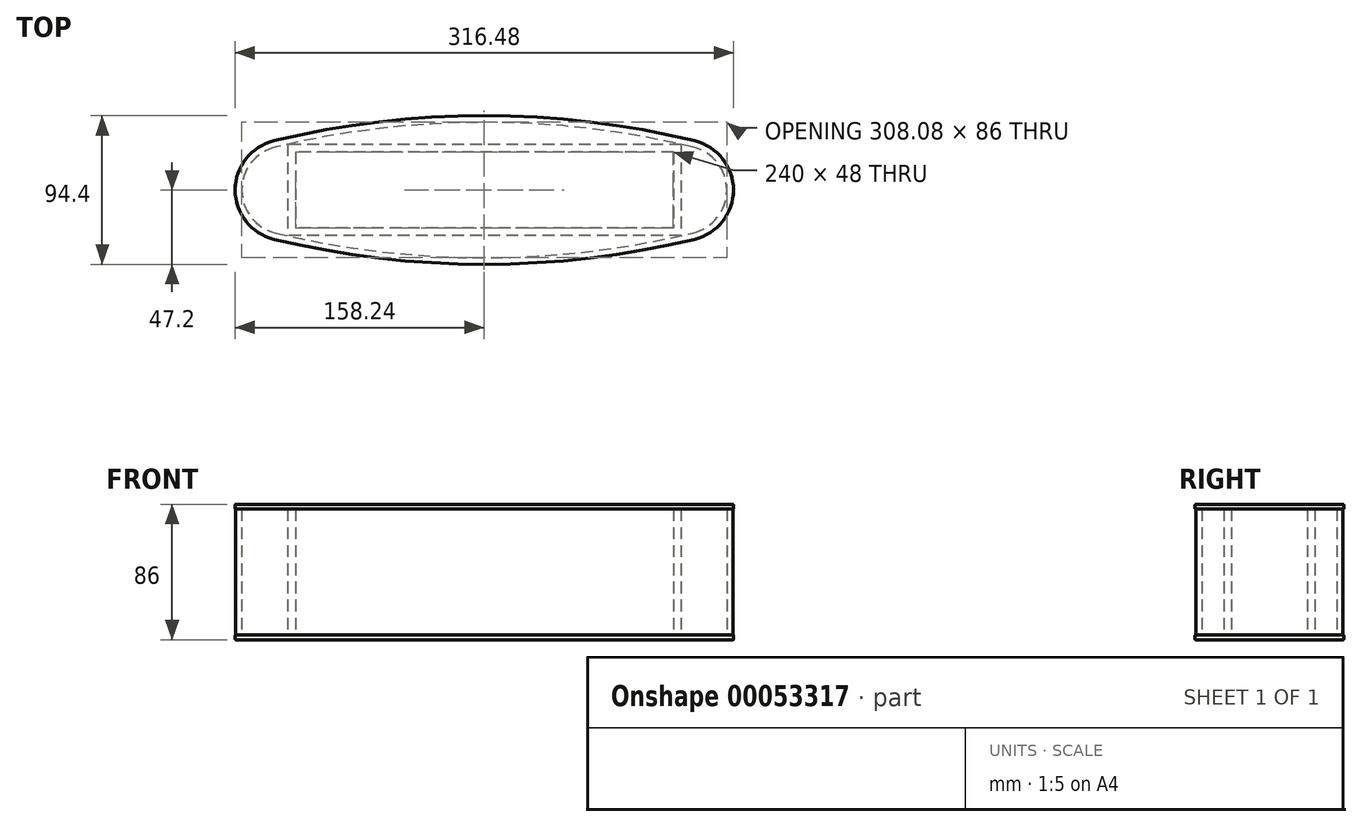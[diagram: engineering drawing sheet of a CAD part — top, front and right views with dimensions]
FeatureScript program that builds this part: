
annotation { "Feature Type Name" : "Feature", "Feature Type Description" : "" }
export const myFeature = defineFeature(function(context is Context, id is Id, definition is map)
    precondition{}
    {
        {
            var Q0;
            Q0=qCreatedBy(makeId("Top.planeOp"),FACE);
            var sketch = newSketch(context, id + "F0", { "sketchPlane" : qUnion([Q0])});
            skLineSegment(sketch, "E0.rect.bottom", {"start": v(120, 24) * mm, "end": v(-120, 24) * mm});
            skLineSegment(sketch, "E0.rect.top", {"start": v(120, -24) * mm, "end": v(-120, -24) * mm});
            skLineSegment(sketch, "E0.rect.left", {"start": v(120, 24) * mm, "end": v(120, -24) * mm});
            skLineSegment(sketch, "E0.rect.right", {"start": v(-120, 24) * mm, "end": v(-120, -24) * mm});
            skPoint(sketch, "E0.rect.middle", {"position": v(0, 0) * mm});
            skLineSegment(sketch, "E1.rect.bottom", {"start": v(125, 29) * mm, "end": v(-125, 29) * mm});
            skLineSegment(sketch, "E1.rect.top", {"start": v(125, -29) * mm, "end": v(-125, -29) * mm});
            skLineSegment(sketch, "E1.rect.left", {"start": v(125, 29) * mm, "end": v(125, -29) * mm});
            skLineSegment(sketch, "E1.rect.right", {"start": v(-125, 29) * mm, "end": v(-125, -29) * mm});
            skArc(sketch, "E2", {"start": v(132.61, 27.22) * mm, "mid": v(0, 43) * mm, "end": v(-132.61, 27.22) * mm});
            skArc(sketch, "E3", {"start": v(-132.61, -27.22) * mm, "mid": v(0, -43) * mm, "end": v(132.61, -27.22) * mm});
            skArc(sketch, "E4", {"start": v(-132.61, 27.22) * mm, "mid": v(-154.04, 0) * mm, "end": v(-132.61, -27.22) * mm});
            skArc(sketch, "E5", {"start": v(132.61, -27.22) * mm, "mid": v(154.04, 0) * mm, "end": v(132.61, 27.22) * mm});
            skArc(sketch, "E6.0", {"start": v(133.5, 30.91) * mm, "mid": v(0, 46.8) * mm, "end": v(-133.5, 30.91) * mm});
            skArc(sketch, "E6.1", {"start": v(133.5, -30.91) * mm, "mid": v(157.84, 0) * mm, "end": v(133.5, 30.91) * mm});
            skArc(sketch, "E6.2", {"start": v(-133.5, -30.91) * mm, "mid": v(0, -46.8) * mm, "end": v(133.5, -30.91) * mm});
            skArc(sketch, "E6.3", {"start": v(-133.5, 30.91) * mm, "mid": v(-157.84, 0) * mm, "end": v(-133.5, -30.91) * mm});
            skArc(sketch, "E7.0", {"start": v(133.6, 31.3) * mm, "mid": v(0, 47.2) * mm, "end": v(-133.6, 31.3) * mm});
            skArc(sketch, "E7.1", {"start": v(133.6, -31.3) * mm, "mid": v(158.24, 0) * mm, "end": v(133.6, 31.3) * mm});
            skArc(sketch, "E7.2", {"start": v(-133.6, -31.3) * mm, "mid": v(0, -47.2) * mm, "end": v(133.6, -31.3) * mm});
            skArc(sketch, "E7.3", {"start": v(-133.6, 31.3) * mm, "mid": v(-158.24, 0) * mm, "end": v(-133.6, -31.3) * mm});
            skSolve(sketch);
        }
        {
            var Q0;
            {var subQ5=sQuery(id+"F0.wireOp",EDGE,"E4");Q0=makeQuery(id+"F0.imprint","IMPRINT",FACE,{"disambiguationData":[TD([[makeQuery(id+"F0.imprint","IMPRINT",EDGE,{"derivedFrom":subQ5}),-1.0]])]});}
            var Q1;
            Q1=makeQuery(id+"F0.imprint","IMPRINT",FACE,{"disambiguationData":[TD([[makeQuery(id+"F0.imprint","IMPRINT",EDGE,{"derivedFrom":sQuery(id+"F0.wireOp",EDGE,"E0.rect.bottom")}),-1.0]])]});
            extrude(context, id + "F1", {"entities" : qUnion([Q0, Q1]), "depth" : 80 * mm});
        }
        {
            var Q0;
            Q0 = qSketchRegion(id + "F0", true);
            var Q1;
            Q1=makeQuery(id+"F1.opExtrude","CAP_FACE",FACE,{"disambiguationData":[OSD([sQuery(id+"F0.wireOp",EDGE,"E2"),sQuery(id+"F0.wireOp",EDGE,"E3"),sQuery(id+"F0.wireOp",EDGE,"E4"),sQuery(id+"F0.wireOp",EDGE,"E5"),sQuery(id+"F0.wireOp",EDGE,"E6.0"),sQuery(id+"F0.wireOp",EDGE,"E6.1"),sQuery(id+"F0.wireOp",EDGE,"E6.2"),sQuery(id+"F0.wireOp",EDGE,"E6.3")])],"isStart":true});
            var Q2;
            {var subQ0=sQuery(id+"F0.wireOp",EDGE,"E1.rect.left");Q2=makeQuery(id+"F0.imprint","IMPRINT",FACE,{"disambiguationData":[TD([[makeQuery(id+"F0.imprint","IMPRINT",EDGE,{"derivedFrom":subQ0}),1.0]])]});}
            var Q3;
            {var subQ0=sQuery(id+"F0.wireOp",EDGE,"E1.rect.bottom");Q3=makeQuery(id+"F0.imprint","IMPRINT",FACE,{"disambiguationData":[TD([[makeQuery(id+"F0.imprint","IMPRINT",EDGE,{"derivedFrom":subQ0}),-1.0]])]});}
            var Q4;
            Q4=makeQuery(id+"F0.imprint","IMPRINT",FACE,{"disambiguationData":[TD([[makeQuery(id+"F0.imprint","IMPRINT",EDGE,{"derivedFrom":sQuery(id+"F0.wireOp",EDGE,"E0.rect.bottom")}),-1.0]])]});
            var Q5;
            Q5=makeQuery(id+"F0.imprint","IMPRINT",FACE,{"disambiguationData":[TD([[makeQuery(id+"F0.imprint","IMPRINT",EDGE,{"derivedFrom":sQuery(id+"F0.wireOp",EDGE,"E0.rect.bottom")}),1.0]])]});
            var Q6;
            {var subQ0=sQuery(id+"F0.wireOp",EDGE,"E1.rect.top");Q6=makeQuery(id+"F0.imprint","IMPRINT",FACE,{"disambiguationData":[TD([[makeQuery(id+"F0.imprint","IMPRINT",EDGE,{"derivedFrom":subQ0}),1.0]])]});}
            var Q7;
            {var subQ0=sQuery(id+"F0.wireOp",EDGE,"E1.rect.right");Q7=makeQuery(id+"F0.imprint","IMPRINT",FACE,{"disambiguationData":[TD([[makeQuery(id+"F0.imprint","IMPRINT",EDGE,{"derivedFrom":subQ0}),-1.0]])]});}
            extrude(context, id + "F2", {"entities" : qUnion([Q0, Q1, Q2, Q3, Q4, Q5, Q6, Q7]), "oppositeDirection" : true, "depth" : 3 * mm});
        }
        {
            var Q0;
            Q0=makeQuery(id+"F2.opExtrude","SWEPT_BODY",BODY,{"disambiguationData":[OSD([sQuery(id+"F0.wireOp",EDGE,"E2"),sQuery(id+"F0.wireOp",EDGE,"E3"),sQuery(id+"F0.wireOp",EDGE,"E4"),sQuery(id+"F0.wireOp",EDGE,"E5"),sQuery(id+"F0.wireOp",EDGE,"E6.0"),sQuery(id+"F0.wireOp",EDGE,"E6.1"),sQuery(id+"F0.wireOp",EDGE,"E6.2"),sQuery(id+"F0.wireOp",EDGE,"E6.3")])]});
            var Q1;
            Q1=makeQuery(id+"F2.opExtrude","SWEPT_BODY",BODY,{"disambiguationData":[OSD([sQuery(id+"F0.wireOp",EDGE,"E6.0"),sQuery(id+"F0.wireOp",EDGE,"E6.1"),sQuery(id+"F0.wireOp",EDGE,"E6.2"),sQuery(id+"F0.wireOp",EDGE,"E6.3"),sQuery(id+"F0.wireOp",EDGE,"E7.0"),sQuery(id+"F0.wireOp",EDGE,"E7.1"),sQuery(id+"F0.wireOp",EDGE,"E7.2"),sQuery(id+"F0.wireOp",EDGE,"E7.3")])]});
            booleanBodies(context, id + "F3", {"operationType" : BooleanOperationType.UNION, "tools" : qUnion([Q0, Q1])});
        }
        {
            var Q0;
            Q0=makeQuery(id+"F2.opExtrude","SWEPT_BODY",BODY,{"disambiguationData":[OSD([sQuery(id+"F0.wireOp",EDGE,"E2"),sQuery(id+"F0.wireOp",EDGE,"E3"),sQuery(id+"F0.wireOp",EDGE,"E4"),sQuery(id+"F0.wireOp",EDGE,"E5")])]});
            var Q1;
            Q1=makeQuery(id+"F2.opExtrude","SWEPT_BODY",BODY,{"disambiguationData":[OSD([sQuery(id+"F0.wireOp",EDGE,"E2"),sQuery(id+"F0.wireOp",EDGE,"E3"),sQuery(id+"F0.wireOp",EDGE,"E4"),sQuery(id+"F0.wireOp",EDGE,"E5"),sQuery(id+"F0.wireOp",EDGE,"E6.0"),sQuery(id+"F0.wireOp",EDGE,"E6.1"),sQuery(id+"F0.wireOp",EDGE,"E6.2"),sQuery(id+"F0.wireOp",EDGE,"E6.3")])]});
            booleanBodies(context, id + "F4", {"operationType" : BooleanOperationType.UNION, "tools" : qUnion([Q0, Q1])});
        }
        {
            var Q0;
            Q0=makeQuery(id+"F1.opExtrude","CAP_FACE",FACE,{"disambiguationData":[OSD([sQuery(id+"F0.wireOp",EDGE,"E2"),sQuery(id+"F0.wireOp",EDGE,"E3"),sQuery(id+"F0.wireOp",EDGE,"E4"),sQuery(id+"F0.wireOp",EDGE,"E5"),sQuery(id+"F0.wireOp",EDGE,"E6.0"),sQuery(id+"F0.wireOp",EDGE,"E6.1"),sQuery(id+"F0.wireOp",EDGE,"E6.2"),sQuery(id+"F0.wireOp",EDGE,"E6.3")])],"isStart":false});
            var sketch = newSketch(context, id + "F5", { "sketchPlane" : qUnion([Q0])});
            skArc(sketch, "E8.0", {"start": v(-133.6, -31.3) * mm, "mid": v(0, -47.2) * mm, "end": v(133.6, -31.3) * mm});
            skArc(sketch, "E9.0", {"start": v(133.6, -31.3) * mm, "mid": v(158.24, 0) * mm, "end": v(133.6, 31.3) * mm});
            skArc(sketch, "E10.0", {"start": v(-133.6, 31.3) * mm, "mid": v(-158.24, 0) * mm, "end": v(-133.6, -31.3) * mm});
            skArc(sketch, "E11.0", {"start": v(133.6, 31.3) * mm, "mid": v(0, 47.2) * mm, "end": v(-133.6, 31.3) * mm});
            skSolve(sketch);
        }
        {
            var Q0;
            Q0 = qSketchRegion(id + "F5", true);
            extrude(context, id + "F6", {"entities" : qUnion([Q0]), "depth" : 3 * mm});
        }
        {
            var Q0;
            Q0=makeQuery(id+"F6.opExtrude","CAP_FACE",FACE,{"disambiguationData":[OSD([sQuery(id+"F5.wireOp",EDGE,"E8.0"),sQuery(id+"F5.wireOp",EDGE,"E9.0"),sQuery(id+"F5.wireOp",EDGE,"E10.0"),sQuery(id+"F5.wireOp",EDGE,"E11.0")])],"isStart":false});
            var Q1;
            {var subQ0=sQuery(id+"F0.wireOp",EDGE,"E6.3");var subQ1=sQuery(id+"F0.wireOp",EDGE,"E6.2");var subQ2=sQuery(id+"F0.wireOp",EDGE,"E6.1");var subQ3=sQuery(id+"F0.wireOp",EDGE,"E6.0");var subQ4=sQuery(id+"F0.wireOp",EDGE,"E5");var subQ5=sQuery(id+"F0.wireOp",EDGE,"E4");var subQ6=sQuery(id+"F0.wireOp",EDGE,"E3");var subQ7=sQuery(id+"F0.wireOp",EDGE,"E2");Q1=makeQuery(id+"F4.opBoolean","MERGE",FACE,{"derivedFrom":[makeQuery(id+"F2.opExtrude","CAP_FACE",FACE,{"disambiguationData":[OSD([subQ7,subQ6,subQ5,subQ4])],"isStart":true}),makeQuery(id+"F3.opBoolean","MERGE",FACE,{"derivedFrom":[makeQuery(id+"F2.opExtrude","CAP_FACE",FACE,{"disambiguationData":[OSD([subQ3,subQ2,subQ1,subQ0,sQuery(id+"F0.wireOp",EDGE,"E7.0"),sQuery(id+"F0.wireOp",EDGE,"E7.1"),sQuery(id+"F0.wireOp",EDGE,"E7.2"),sQuery(id+"F0.wireOp",EDGE,"E7.3")])],"isStart":true}),makeQuery(id+"F2.opExtrude","CAP_FACE",FACE,{"disambiguationData":[OSD([subQ7,subQ6,subQ5,subQ4,subQ3,subQ2,subQ1,subQ0])],"isStart":true})]})]});}
            var Q2;
            Q2=makeQuery(id+"F6.opExtrude","CAP_FACE",FACE,{"disambiguationData":[OSD([sQuery(id+"F5.wireOp",EDGE,"E8.0"),sQuery(id+"F5.wireOp",EDGE,"E9.0"),sQuery(id+"F5.wireOp",EDGE,"E10.0"),sQuery(id+"F5.wireOp",EDGE,"E11.0")])],"isStart":true});
            var Q3;
            {var subQ0=sQuery(id+"F0.wireOp",EDGE,"E6.3");var subQ1=sQuery(id+"F0.wireOp",EDGE,"E6.2");var subQ2=sQuery(id+"F0.wireOp",EDGE,"E6.1");var subQ3=sQuery(id+"F0.wireOp",EDGE,"E6.0");var subQ4=sQuery(id+"F0.wireOp",EDGE,"E5");var subQ5=sQuery(id+"F0.wireOp",EDGE,"E4");var subQ6=sQuery(id+"F0.wireOp",EDGE,"E3");var subQ7=sQuery(id+"F0.wireOp",EDGE,"E2");Q3=makeQuery(id+"F4.opBoolean","MERGE",FACE,{"derivedFrom":[makeQuery(id+"F2.opExtrude","CAP_FACE",FACE,{"disambiguationData":[OSD([subQ7,subQ6,subQ5,subQ4])],"isStart":false}),makeQuery(id+"F3.opBoolean","MERGE",FACE,{"derivedFrom":[makeQuery(id+"F2.opExtrude","CAP_FACE",FACE,{"disambiguationData":[OSD([subQ3,subQ2,subQ1,subQ0,sQuery(id+"F0.wireOp",EDGE,"E7.0"),sQuery(id+"F0.wireOp",EDGE,"E7.1"),sQuery(id+"F0.wireOp",EDGE,"E7.2"),sQuery(id+"F0.wireOp",EDGE,"E7.3")])],"isStart":false}),makeQuery(id+"F2.opExtrude","CAP_FACE",FACE,{"disambiguationData":[OSD([subQ7,subQ6,subQ5,subQ4,subQ3,subQ2,subQ1,subQ0])],"isStart":false})]})]});}
            fillet(context, id + "F7", {"entities" : qUnion([Q0, Q1, Q2, Q3]), "radius" : 0.4 * mm, "tangentPropagation" : true, "allowEdgeOverflow" : false});
        }
    });
